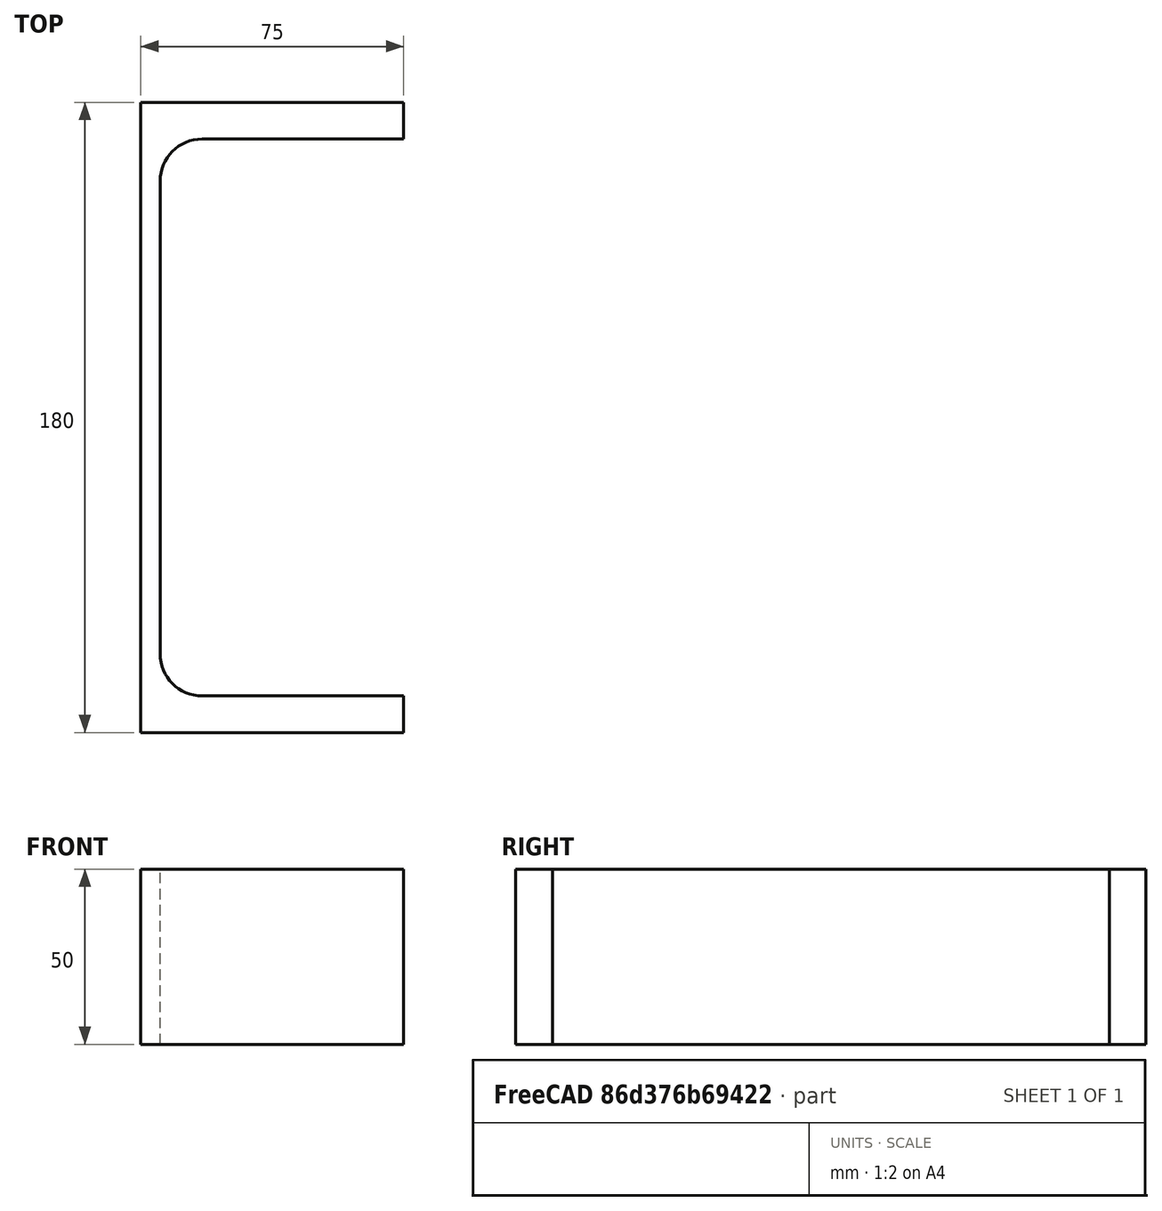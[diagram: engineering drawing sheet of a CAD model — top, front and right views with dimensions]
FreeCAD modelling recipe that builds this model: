
FCSTD DOCUMENT  (FreeCAD 0.20R29410 (Git))
Label: UPE-Profile 180 DIN1026-2 S235JR
License: All rights reserved
LicenseURL: http://en.wikipedia.org/wiki/All_rights_reserved
objects: Sketcher::SketchObject×1, Part::Extrusion×1
note: 2 computed .brp shape members not serialized (recipe doc carries the construction recipe); baked Part::Feature solids carry a one-line shape summary decoded from their .brp

FEATURE [Sketcher::SketchObject] Sketch
  FullyConstrained = true
  MapMode = 5
  sketch-geometry (10):
    g0: LineSegment StartX=5.5 StartY=-67.5 StartZ=0 EndX=5.5 EndY=67.5 EndZ=0
    g1: LineSegment StartX=17.5 StartY=79.5 StartZ=0 EndX=75 EndY=79.5 EndZ=0
    g2: LineSegment StartX=75 StartY=79.5 StartZ=0 EndX=75 EndY=90 EndZ=0
    g3: LineSegment StartX=75 StartY=-90 StartZ=0 EndX=75 EndY=-79.5 EndZ=0
    g4: LineSegment StartX=75 StartY=-79.5 StartZ=0 EndX=17.5 EndY=-79.5 EndZ=0
    g5: ArcOfCircle CenterX=17.5 CenterY=67.5 CenterZ=0 NormalX=0 NormalY=0 NormalZ=1 AngleXU=0 Radius=12 StartAngle=1.5708 EndAngle=3.14159
    g6: ArcOfCircle CenterX=17.5 CenterY=-67.5 CenterZ=0 NormalX=0 NormalY=0 NormalZ=1 AngleXU=0 Radius=12 StartAngle=3.14159 EndAngle=4.71239
    g7: LineSegment StartX=75 StartY=-90 StartZ=0 EndX=0 EndY=-90 EndZ=0
    g8: LineSegment StartX=0 StartY=-90 StartZ=0 EndX=0 EndY=90 EndZ=0
    g9: LineSegment StartX=0 StartY=90 StartZ=0 EndX=75 EndY=90 EndZ=0
  constraints (27):
    c: Vertical(g0)
    c: Coincident(g2,g1)
    c: Vertical(g2)
    c: Vertical(g3)
    c: Coincident(g4,g3)
    c: Horizontal(g4)
    c: Tangent(g1,g5) = 1.5708
    c: Tangent(g0,g5) = 1.5708
    c: Tangent(g0,g6) = 1.5708
    c: Tangent(g4,g6) = 1.5708
    c: Symmetric(g2,g3,g-1)
    c: DistanceY(g2) = 10.5
    c: Radius(g5) = 12
    c: Coincident(g3,g7)
    c: PointOnObject(g7,g-2)
    c: Horizontal(g7)
    c: Coincident(g7,g8)
    c: PointOnObject(g8,g-2)
    c: Coincident(g8,g9)
    c: Coincident(g9,g2)
    c: Horizontal(g9)
    c: Distance(g-1,g0) = 5.5
    c: DistanceX(g9,g9) = 75
    c: Horizontal(g1)
    c: Equal(g3,g2)
    c: Equal(g5,g6)
    c: DistanceY(g3,g2) = 180
FEATURE [Part::Extrusion] Extrude  label="UPE-Profile 180 DIN1026-2 S235JR"
  Base = -> Sketch
  Dir = (0,0,50)
  DirMode = 0
  FaceMakerClass = Part::FaceMakerExtrusion
  LengthFwd = 0
  LengthRev = 0
  Solid = true
  Symmetric = false
